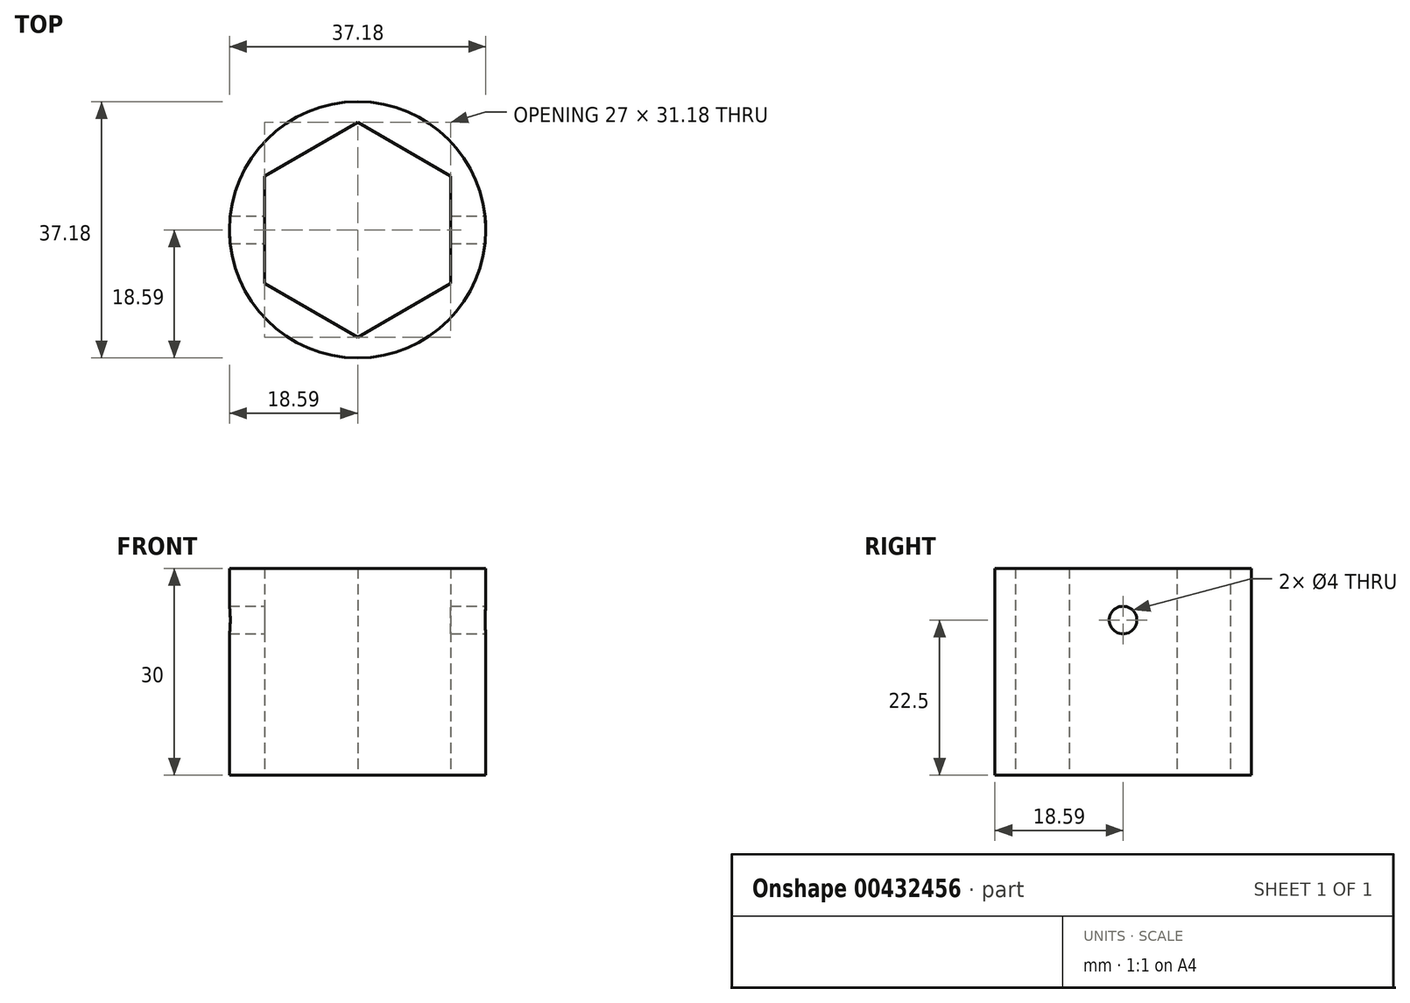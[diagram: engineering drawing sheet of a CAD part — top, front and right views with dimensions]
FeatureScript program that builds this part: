
annotation { "Feature Type Name" : "Feature", "Feature Type Description" : "" }
export const myFeature = defineFeature(function(context is Context, id is Id, definition is map)
    precondition{}
    {
        {
            var Q0;
            Q0=qCreatedBy(makeId("Top.planeOp"),FACE);
            var sketch = newSketch(context, id + "F0", { "sketchPlane" : qUnion([Q0])});
            skCircle(sketch, "E0.cCircle", {"center": v(0, 0) * mm, "radius": 13.5 * mm, "construction": true});
            skLineSegment(sketch, "E0.0", {"start": v(13.5, 7.8) * mm, "end": v(13.5, -7.8) * mm});
            skLineSegment(sketch, "E0.1", {"start": v(13.5, -7.8) * mm, "end": v(0, -15.59) * mm});
            skLineSegment(sketch, "E0.2", {"start": v(0, -15.59) * mm, "end": v(-13.5, -7.8) * mm});
            skLineSegment(sketch, "E0.3", {"start": v(-13.5, -7.8) * mm, "end": v(-13.5, 7.8) * mm});
            skLineSegment(sketch, "E0.4", {"start": v(-13.5, 7.8) * mm, "end": v(0, 15.59) * mm});
            skLineSegment(sketch, "E0.5", {"start": v(0, 15.59) * mm, "end": v(13.5, 7.8) * mm});
            skPoint(sketch, "E0.0.midPoint", {"position": v(13.5, 0) * mm});
            skCircle(sketch, "E1", {"center": v(0, 0) * mm, "radius": 18.59 * mm});
            skLineSegment(sketch, "E2", {"start": v(0, -15.59) * mm, "end": v(0, -18.59) * mm, "construction": true});
            skSolve(sketch);
        }
        {
            var Q0;
            Q0=makeQuery(id+"F0.imprint","IMPRINT",FACE,{"disambiguationData":[TD([[makeQuery(id+"F0.imprint","IMPRINT",EDGE,{"derivedFrom":sQuery(id+"F0.wireOp",EDGE,"E0.0")}),1.0]])]});
            extrude(context, id + "F1", {"entities" : qUnion([Q0]), "depth" : 30 * mm});
        }
        {
            var Q0;
            Q0=makeQuery(id+"F1.opExtrude","SWEPT_FACE",FACE,{"disambiguationData":[OSD([sQuery(id+"F0.wireOp",EDGE,"E0.3")])]});
            var sketch = newSketch(context, id + "F2", { "sketchPlane" : qUnion([Q0])});
            skLineSegment(sketch, "E3", {"start": v(0, 30) * mm, "end": v(0, 0) * mm, "construction": true});
            skCircle(sketch, "E4", {"center": v(0, 22.5) * mm, "radius": 2 * mm});
            skSolve(sketch);
        }
        {
            var Q0;
            Q0=makeQuery(id+"F2.imprint","IMPRINT",FACE,{"disambiguationData":[TD([[makeQuery(id+"F2.imprint","IMPRINT",EDGE,{"derivedFrom":sQuery(id+"F2.wireOp",EDGE,"gcZB8QbN-DCT3-5Kpt-CMNm-CBXJMdyravBy")}),1.0]])]});
            var Q1;
            Q1=makeQuery(id+"F2.imprint","IMPRINT",FACE,{"disambiguationData":[TD([[makeQuery(id+"F2.imprint","IMPRINT",EDGE,{"derivedFrom":sQuery(id+"F2.wireOp",EDGE,"E4")}),1.0]])]});
            extrude(context, id + "F3", {"entities" : qUnion([Q0, Q1]), "operationType" : NewBodyOperationType.REMOVE, "endBound" : BoundingType.THROUGH_ALL, "oppositeDirection" : true, "depth" : 25 * mm, "hasSecondDirection" : true, "secondDirectionBound" : SecondDirectionBoundingType.THROUGH_ALL, "secondDirectionOppositeDirection" : false, "secondDirectionDepth" : 25 * mm});
        }
    });
